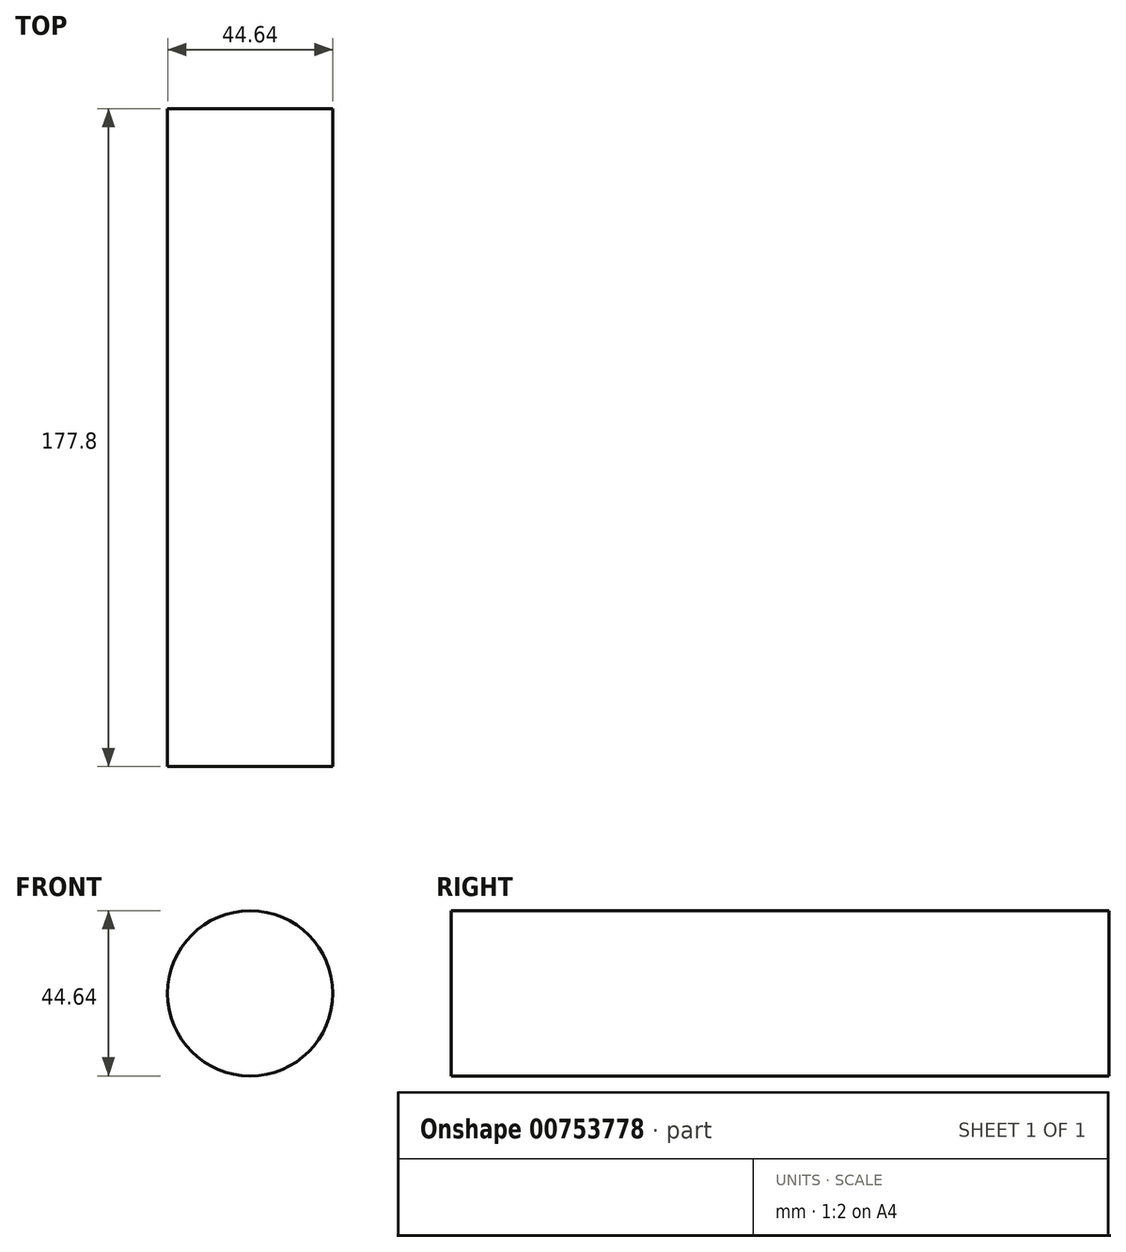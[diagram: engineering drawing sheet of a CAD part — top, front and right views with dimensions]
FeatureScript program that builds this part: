
annotation { "Feature Type Name" : "Feature", "Feature Type Description" : "" }
export const myFeature = defineFeature(function(context is Context, id is Id, definition is map)
    precondition{}
    {
        {
            var Q0;
            Q0=qCreatedBy(makeId("Front.planeOp"),FACE);
            var sketch = newSketch(context, id + "F0", { "sketchPlane" : qUnion([Q0])});
            skCircle(sketch, "E0", {"center": v(0, 0) * mm, "radius": 22.32 * mm});
            skSolve(sketch);
        }
        {
            var Q0;
            Q0=makeQuery(id+"F0.imprint","IMPRINT",FACE,{"disambiguationData":[TD([[makeQuery(id+"F0.imprint","IMPRINT",EDGE,{"derivedFrom":sQuery(id+"F0.wireOp",EDGE,"E0")}),1.0]])]});
            extrude(context, id + "F1", {"entities" : qUnion([Q0]), "depth" : 177.8 * mm, "offsetDistance" : 25.4 * mm});
        }
    });
